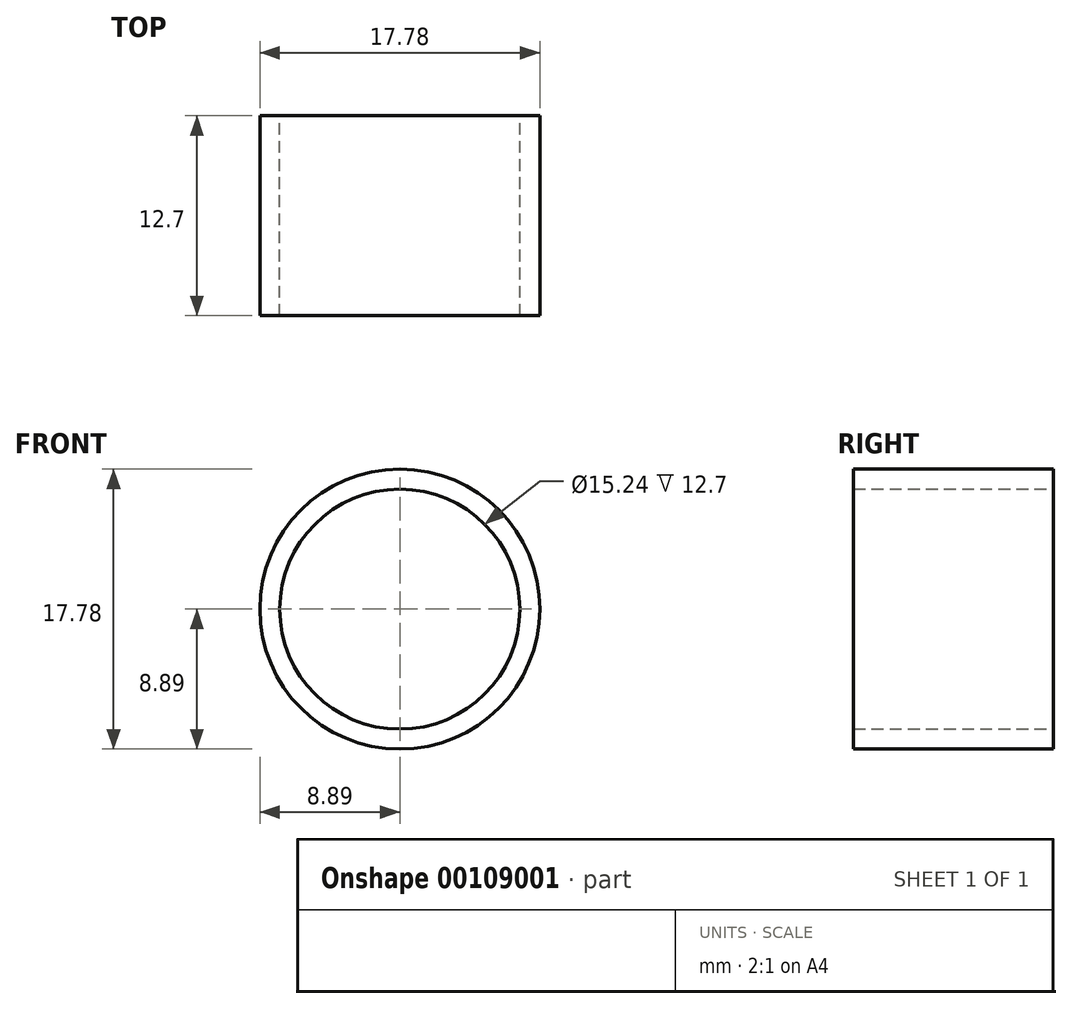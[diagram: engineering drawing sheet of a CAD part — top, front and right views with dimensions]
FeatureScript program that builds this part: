
annotation { "Feature Type Name" : "Feature", "Feature Type Description" : "" }
export const myFeature = defineFeature(function(context is Context, id is Id, definition is map)
    precondition{}
    {
        {
            var Q0;
            Q0=qCreatedBy(makeId("Front.planeOp"),FACE);
            var sketch = newSketch(context, id + "F0", { "sketchPlane" : qUnion([Q0])});
            skCircle(sketch, "E0", {"center": v(0, 0) * mm, "radius": 8.9 * mm});
            skCircle(sketch, "E1", {"center": v(0, 0) * mm, "radius": 7.62 * mm});
            skSolve(sketch);
        }
        {
            var Q0;
            Q0=makeQuery(id+"F0.imprint","IMPRINT",FACE,{"disambiguationData":[TD([[makeQuery(id+"F0.imprint","IMPRINT",EDGE,{"derivedFrom":sQuery(id+"F0.wireOp",EDGE,"E0")}),1.0]])]});
            extrude(context, id + "F1", {"entities" : qUnion([Q0]), "depth" : 12.7 * mm});
        }
    });
